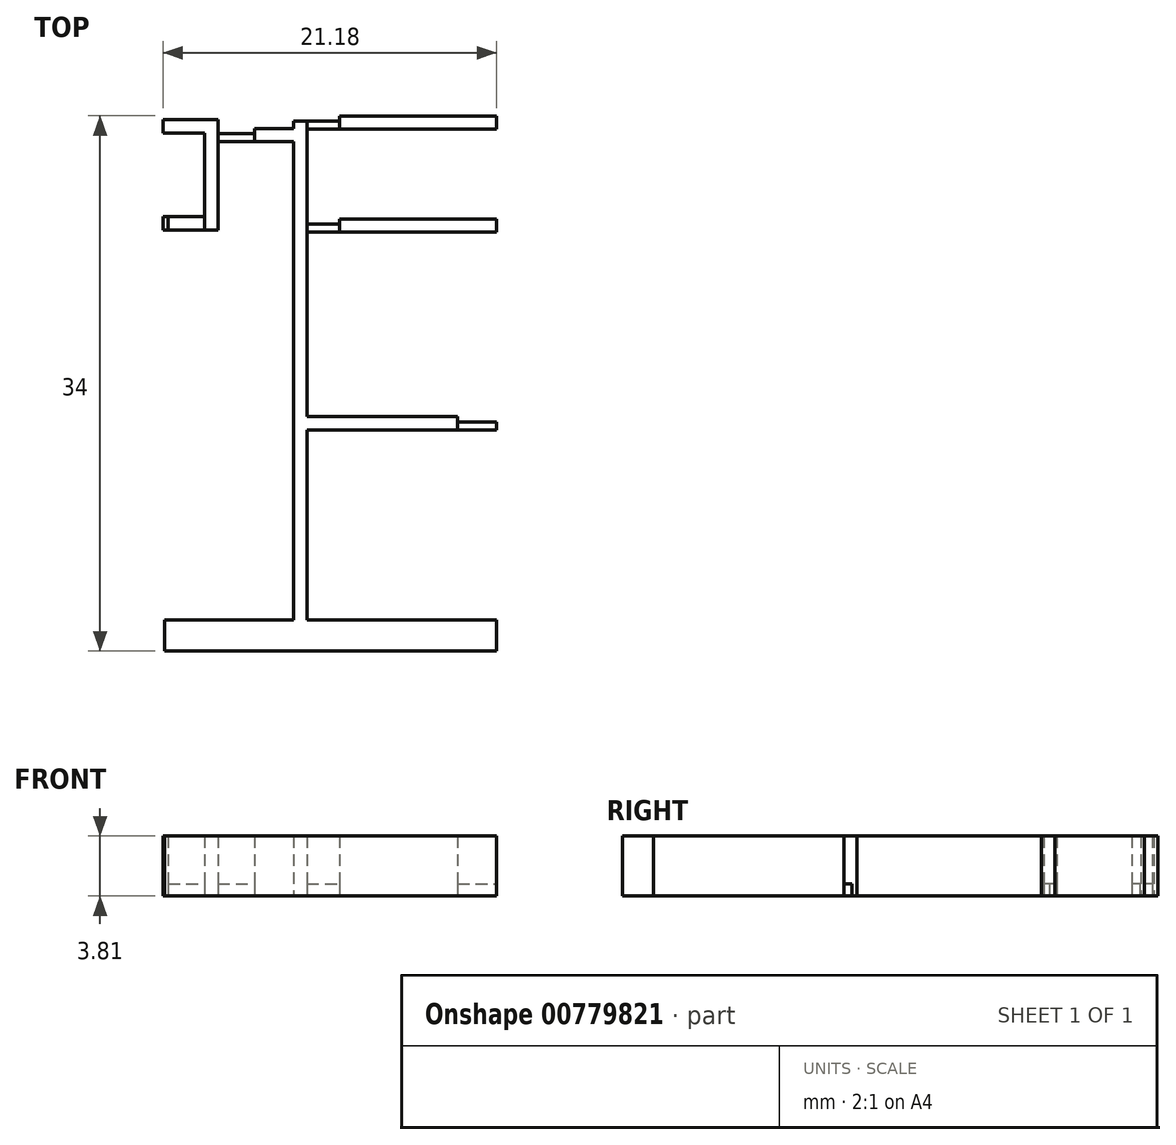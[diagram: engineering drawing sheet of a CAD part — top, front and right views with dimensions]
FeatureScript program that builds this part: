
annotation { "Feature Type Name" : "Feature", "Feature Type Description" : "" }
export const myFeature = defineFeature(function(context is Context, id is Id, definition is map)
    precondition{}
    {
        {
            var Q0;
            Q0=qCreatedBy(makeId("Top.planeOp"),FACE);
            var sketch = newSketch(context, id + "F0", { "sketchPlane" : qUnion([Q0])});
            skLineSegment(sketch, "E0.bottom", {"start": v(6.1, -61.3) * mm, "end": v(-3.48, -61.3) * mm});
            skLineSegment(sketch, "E0.top", {"start": v(6.1, -62.15) * mm, "end": v(-3.48, -62.15) * mm});
            skLineSegment(sketch, "E0.left", {"start": v(6.1, -61.3) * mm, "end": v(6.1, -62.15) * mm});
            skLineSegment(sketch, "E0.right", {"start": v(-3.48, -61.3) * mm, "end": v(-3.48, -62.15) * mm});
            skLineSegment(sketch, "E1.bottom", {"start": v(-3.47, -76.15) * mm, "end": v(-4.3, -76.15) * mm});
            skLineSegment(sketch, "E1.top", {"start": v(-3.47, -42.53) * mm, "end": v(-4.3, -42.53) * mm});
            skLineSegment(sketch, "E1.left", {"start": v(-3.47, -76.15) * mm, "end": v(-3.47, -42.53) * mm});
            skLineSegment(sketch, "E1.right", {"start": v(-4.3, -76.15) * mm, "end": v(-4.3, -42.53) * mm});
            skLineSegment(sketch, "E2.bottom", {"start": v(-1.38, -49.59) * mm, "end": v(8.58, -49.59) * mm});
            skLineSegment(sketch, "E2.top", {"start": v(-1.38, -48.75) * mm, "end": v(8.58, -48.75) * mm});
            skLineSegment(sketch, "E2.left", {"start": v(-1.38, -49.59) * mm, "end": v(-1.38, -48.75) * mm});
            skLineSegment(sketch, "E2.right", {"start": v(8.58, -49.59) * mm, "end": v(8.58, -48.75) * mm});
            skLineSegment(sketch, "E3.bottom", {"start": v(-1.38, -42.2) * mm, "end": v(8.57, -42.2) * mm});
            skLineSegment(sketch, "E3.top", {"start": v(-1.38, -43.04) * mm, "end": v(8.57, -43.04) * mm});
            skLineSegment(sketch, "E3.left", {"start": v(-1.38, -42.2) * mm, "end": v(-1.38, -43.04) * mm});
            skLineSegment(sketch, "E3.right", {"start": v(8.57, -42.2) * mm, "end": v(8.57, -43.04) * mm});
            skLineSegment(sketch, "E4.bottom", {"start": v(8.57, -42.2) * mm, "end": v(8.57, -42.2) * mm});
            skLineSegment(sketch, "E5.bottom", {"start": v(-4.3, -43.01) * mm, "end": v(-6.8, -43.01) * mm});
            skLineSegment(sketch, "E5.top", {"start": v(-4.3, -43.85) * mm, "end": v(-6.8, -43.85) * mm});
            skLineSegment(sketch, "E5.left", {"start": v(-4.3, -43.01) * mm, "end": v(-4.3, -43.85) * mm});
            skLineSegment(sketch, "E5.right", {"start": v(-6.8, -43.01) * mm, "end": v(-6.8, -43.85) * mm});
            skLineSegment(sketch, "E6.bottom", {"start": v(-12.29, -49.45) * mm, "end": v(-12.6, -49.45) * mm});
            skLineSegment(sketch, "E6.top", {"start": v(-12.29, -48.6) * mm, "end": v(-12.6, -48.6) * mm});
            skLineSegment(sketch, "E6.left", {"start": v(-12.29, -49.45) * mm, "end": v(-12.29, -48.6) * mm});
            skLineSegment(sketch, "E6.right", {"start": v(-12.6, -49.45) * mm, "end": v(-12.6, -48.6) * mm});
            skLineSegment(sketch, "E7.bottom", {"start": v(-9.12, -49.45) * mm, "end": v(-9.96, -49.45) * mm});
            skLineSegment(sketch, "E7.top", {"start": v(-9.12, -43.28) * mm, "end": v(-9.96, -43.28) * mm});
            skLineSegment(sketch, "E7.left", {"start": v(-9.12, -49.45) * mm, "end": v(-9.12, -43.28) * mm});
            skLineSegment(sketch, "E7.right", {"start": v(-9.96, -49.45) * mm, "end": v(-9.96, -43.28) * mm});
            skLineSegment(sketch, "E8.bottom", {"start": v(-9.12, -43.28) * mm, "end": v(-12.6, -43.28) * mm});
            skLineSegment(sketch, "E8.top", {"start": v(-9.12, -42.45) * mm, "end": v(-12.6, -42.45) * mm});
            skLineSegment(sketch, "E8.left", {"start": v(-9.12, -43.28) * mm, "end": v(-9.12, -42.45) * mm});
            skLineSegment(sketch, "E9.bottom", {"start": v(8.58, -76.2) * mm, "end": v(-12.52, -76.2) * mm});
            skLineSegment(sketch, "E9.top", {"start": v(8.58, -74.23) * mm, "end": v(-12.52, -74.23) * mm});
            skLineSegment(sketch, "E9.left", {"start": v(8.58, -76.2) * mm, "end": v(8.58, -74.23) * mm});
            skLineSegment(sketch, "E10", {"start": v(-12.6, -42.45) * mm, "end": v(-12.6, -43.28) * mm});
            skLineSegment(sketch, "E11", {"start": v(-12.52, -74.23) * mm, "end": v(-12.52, -76.2) * mm});
            skSolve(sketch);
        }
        {
            var Q0;
            Q0=qSketchRegion(id+"F0",true);
            extrude(context, id + "F1", {"entities" : qUnion([Q0]), "depth" : 3.8 * mm, "offsetDistance" : 25.4 * mm});
        }
        {
            var Q0;
            Q0=qCreatedBy(makeId("Top.planeOp"),FACE);
            var sketch = newSketch(context, id + "F2", { "sketchPlane" : qUnion([Q0])});
            skLineSegment(sketch, "E12.bottom", {"start": v(-12.29, -48.6) * mm, "end": v(-9.96, -48.6) * mm});
            skLineSegment(sketch, "E12.top", {"start": v(-12.29, -49.45) * mm, "end": v(-9.96, -49.45) * mm});
            skLineSegment(sketch, "E12.left", {"start": v(-12.29, -48.6) * mm, "end": v(-12.29, -49.45) * mm});
            skLineSegment(sketch, "E12.right", {"start": v(-9.96, -48.6) * mm, "end": v(-9.96, -49.45) * mm});
            skLineSegment(sketch, "E13.bottom", {"start": v(-9.12, -43.34) * mm, "end": v(-6.8, -43.34) * mm});
            skLineSegment(sketch, "E13.top", {"start": v(-9.12, -43.85) * mm, "end": v(-6.8, -43.85) * mm});
            skLineSegment(sketch, "E13.left", {"start": v(-9.12, -43.34) * mm, "end": v(-9.12, -43.85) * mm});
            skLineSegment(sketch, "E13.right", {"start": v(-6.8, -43.34) * mm, "end": v(-6.8, -43.85) * mm});
            skLineSegment(sketch, "E14.bottom", {"start": v(-3.47, -42.53) * mm, "end": v(-1.38, -42.53) * mm});
            skLineSegment(sketch, "E14.top", {"start": v(-3.47, -43.04) * mm, "end": v(-1.38, -43.04) * mm});
            skLineSegment(sketch, "E14.left", {"start": v(-3.47, -42.53) * mm, "end": v(-3.47, -43.04) * mm});
            skLineSegment(sketch, "E14.right", {"start": v(-1.38, -42.53) * mm, "end": v(-1.38, -43.04) * mm});
            skLineSegment(sketch, "E15.bottom", {"start": v(-3.47, -49.08) * mm, "end": v(-1.38, -49.08) * mm});
            skLineSegment(sketch, "E15.top", {"start": v(-3.47, -49.59) * mm, "end": v(-1.38, -49.59) * mm});
            skLineSegment(sketch, "E15.left", {"start": v(-3.47, -49.08) * mm, "end": v(-3.47, -49.59) * mm});
            skLineSegment(sketch, "E15.right", {"start": v(-1.38, -49.08) * mm, "end": v(-1.38, -49.59) * mm});
            skLineSegment(sketch, "E16.bottom", {"start": v(6.1, -61.64) * mm, "end": v(8.58, -61.64) * mm});
            skLineSegment(sketch, "E16.top", {"start": v(6.1, -62.15) * mm, "end": v(8.58, -62.15) * mm});
            skLineSegment(sketch, "E16.left", {"start": v(6.1, -61.64) * mm, "end": v(6.1, -62.15) * mm});
            skLineSegment(sketch, "E16.right", {"start": v(8.58, -61.64) * mm, "end": v(8.58, -62.15) * mm});
            skSolve(sketch);
        }
        {
            var Q0;
            Q0 = qSketchRegion(id + "F2", true);
            extrude(context, id + "F3", {"entities" : qUnion([Q0]), "depth" : 0.76 * mm, "offsetDistance" : 25.4 * mm});
        }
    });
